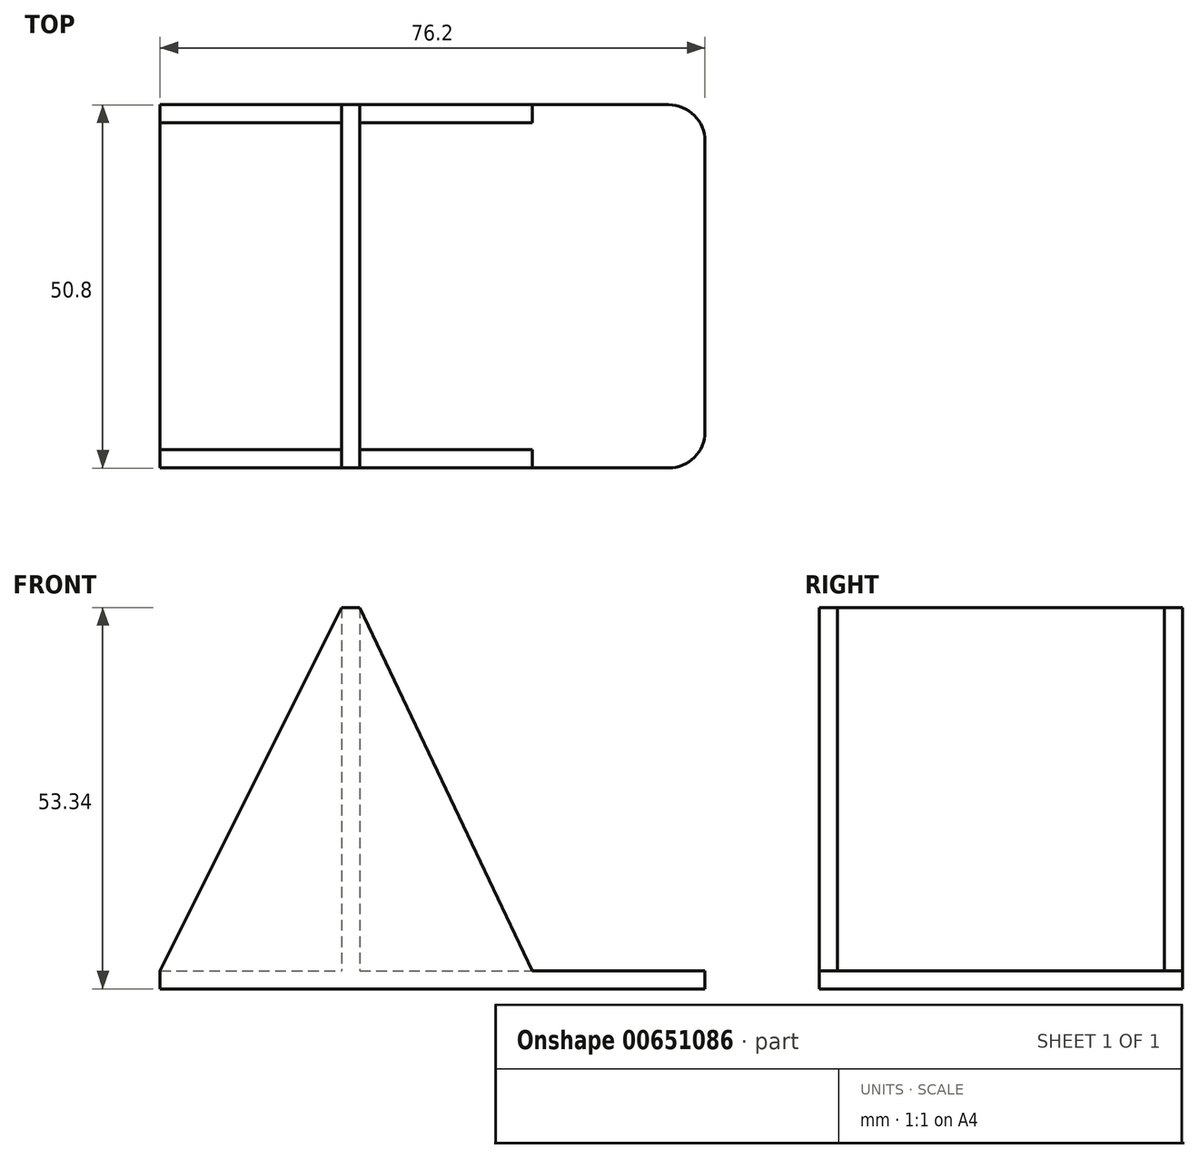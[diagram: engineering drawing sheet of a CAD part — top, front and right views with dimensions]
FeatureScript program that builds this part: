
annotation { "Feature Type Name" : "Feature", "Feature Type Description" : "" }
export const myFeature = defineFeature(function(context is Context, id is Id, definition is map)
    precondition{}
    {
        {
            var Q0;
            Q0=qCreatedBy(makeId("Top.planeOp"),FACE);
            var sketch = newSketch(context, id + "F0", { "sketchPlane" : qUnion([Q0])});
            skLineSegment(sketch, "E0.bottom", {"start": v(-22.34, 32.12) * mm, "end": v(53.86, 32.12) * mm});
            skLineSegment(sketch, "E0.top", {"start": v(-22.34, -18.68) * mm, "end": v(53.86, -18.68) * mm});
            skLineSegment(sketch, "E0.left", {"start": v(-22.34, 32.12) * mm, "end": v(-22.34, -18.68) * mm});
            skLineSegment(sketch, "E0.right", {"start": v(53.86, 32.12) * mm, "end": v(53.86, -18.68) * mm});
            skLineSegment(sketch, "E1.bottom", {"start": v(3.06, 32.12) * mm, "end": v(5.6, 32.12) * mm});
            skLineSegment(sketch, "E1.top", {"start": v(3.06, -18.68) * mm, "end": v(5.6, -18.68) * mm});
            skLineSegment(sketch, "E1.left", {"start": v(3.06, 32.12) * mm, "end": v(3.06, -18.68) * mm});
            skLineSegment(sketch, "E1.right", {"start": v(5.6, 32.12) * mm, "end": v(5.6, -18.68) * mm});
            skSolve(sketch);
        }
        {
            var Q0;
            {var subQ3=sQuery(id+"F0.wireOp",EDGE,"E1.left");var subQ8=makeQuery(id+"F0.imprint","IMPRINT",EDGE,{"derivedFrom":subQ3});var subQ10=sQuery(id+"F0.wireOp",EDGE,"E0.left");var subQ11=sQuery(id+"F0.wireOp",EDGE,"E0.right");Q0=qUnion([makeQuery(id+"F0.imprint","IMPRINT",FACE,{"disambiguationData":[TD([[makeQuery(id+"F0.imprint","IMPRINT",EDGE,{"derivedFrom":subQ11}),-1.0]])]}),makeQuery(id+"F0.imprint","IMPRINT",FACE,{"disambiguationData":[TD([[makeQuery(id+"F0.imprint","IMPRINT",EDGE,{"derivedFrom":subQ10}),1.0]])]}),makeQuery(id+"F0.imprint","IMPRINT",FACE,{"disambiguationData":[TD([[subQ8,1.0]])]})]);}
            extrude(context, id + "F1", {"entities" : qUnion([Q0]), "oppositeDirection" : true, "depth" : 2.54 * mm, "offsetDistance" : 25.4 * mm});
        }
        {
            var Q0;
            {var subQ2=sQuery(id+"F0.wireOp",EDGE,"E1.left");Q0=makeQuery(id+"F0.imprint","IMPRINT",FACE,{"disambiguationData":[TD([[makeQuery(id+"F0.imprint","IMPRINT",EDGE,{"derivedFrom":subQ2}),1.0]])]});}
            extrude(context, id + "F2", {"entities" : qUnion([Q0]), "operationType" : NewBodyOperationType.ADD, "depth" : 50.8 * mm, "offsetDistance" : 25.4 * mm});
        }
        {
            var Q0;
            {var subQ0=sQuery(id+"F0.wireOp",EDGE,"E0.top");Q0=makeQuery(id+"F2.boolean.opBoolean","MERGE",FACE,{"derivedFrom":[makeQuery(id+"F1.opExtrude","SWEPT_FACE",FACE,{"disambiguationData":[OSD([subQ0])]}),makeQuery(id+"F2.opExtrude","SWEPT_FACE",FACE,{"disambiguationData":[OSD([subQ0])]})]});}
            var sketch = newSketch(context, id + "F3", { "sketchPlane" : qUnion([Q0])});
            skLineSegment(sketch, "E2", {"start": v(-22.34, 0) * mm, "end": v(3.06, 50.8) * mm});
            skLineSegment(sketch, "E3", {"start": v(3.06, 50.8) * mm, "end": v(5.6, 50.8) * mm});
            skLineSegment(sketch, "E4", {"start": v(5.6, 50.8) * mm, "end": v(29.73, 0) * mm});
            skSolve(sketch);
        }
        {
            var Q0;
            Q0=makeQuery(id+"F3.imprint","IMPRINT",FACE,{"disambiguationData":[TD([[makeQuery(id+"F3.imprint","IMPRINT",EDGE,{"derivedFrom":sQuery(id+"F3.wireOp",EDGE,"E2")}),-1.0]])]});
            var Q1;
            {var subQ0=sQuery(id+"F3.wireOp",EDGE,"E4");Q1=makeQuery(id+"F3.imprint","IMPRINT",FACE,{"disambiguationData":[TD([[makeQuery(id+"F3.imprint","IMPRINT",EDGE,{"derivedFrom":subQ0}),-1.0]])]});}
            extrude(context, id + "F4", {"entities" : qUnion([Q0, Q1]), "operationType" : NewBodyOperationType.ADD, "oppositeDirection" : true, "depth" : 2.54 * mm, "offsetDistance" : 25.4 * mm});
        }
        {
            var Q0;
            {var subQ0=sQuery(id+"F0.wireOp",EDGE,"E0.bottom");Q0=makeQuery(id+"F2.boolean.opBoolean","MERGE",FACE,{"derivedFrom":[makeQuery(id+"F1.opExtrude","SWEPT_FACE",FACE,{"disambiguationData":[OSD([subQ0])]}),makeQuery(id+"F2.opExtrude","SWEPT_FACE",FACE,{"disambiguationData":[OSD([subQ0])]})]});}
            var sketch = newSketch(context, id + "F5", { "sketchPlane" : qUnion([Q0])});
            skLineSegment(sketch, "E5", {"start": v(-5.6, 50.8) * mm, "end": v(-29.73, 0) * mm});
            skLineSegment(sketch, "E6", {"start": v(-5.6, 50.8) * mm, "end": v(-3.06, 50.8) * mm});
            skLineSegment(sketch, "E7", {"start": v(-3.06, 50.8) * mm, "end": v(22.34, 0) * mm});
            skLineSegment(sketch, "E8", {"start": v(22.34, 0) * mm, "end": v(-29.73, 0) * mm});
            skSolve(sketch);
        }
        {
            var Q0;
            {var subQ0=sQuery(id+"F5.wireOp",EDGE,"E7");Q0=makeQuery(id+"F5.imprint","IMPRINT",FACE,{"disambiguationData":[TD([[makeQuery(id+"F5.imprint","IMPRINT",EDGE,{"derivedFrom":subQ0}),-1.0]])]});}
            var Q1;
            {var subQ0=sQuery(id+"F5.wireOp",EDGE,"E5");Q1=makeQuery(id+"F5.imprint","IMPRINT",FACE,{"disambiguationData":[TD([[makeQuery(id+"F5.imprint","IMPRINT",EDGE,{"derivedFrom":subQ0}),1.0]])]});}
            extrude(context, id + "F6", {"entities" : qUnion([Q0, Q1]), "operationType" : NewBodyOperationType.ADD, "oppositeDirection" : true, "depth" : 2.54 * mm, "offsetDistance" : 25.4 * mm});
        }
        {
            var Q0;
            Q0=makeQuery(id+"F1.opExtrude","SWEPT_EDGE",EDGE,{"disambiguationData":[OSD([sQuery(id+"F0.wireOp",EDGE,"E0.top"),sQuery(id+"F0.wireOp",EDGE,"E0.right")])]});
            var Q1;
            Q1=makeQuery(id+"F1.opExtrude","SWEPT_EDGE",EDGE,{"disambiguationData":[OSD([sQuery(id+"F0.wireOp",EDGE,"E0.bottom"),sQuery(id+"F0.wireOp",EDGE,"E0.right")])]});
            fillet(context, id + "F7", {"entities" : qUnion([Q0, Q1]), "radius" : 5.08 * mm, "tangentPropagation" : true, "allowEdgeOverflow" : false});
        }
    });
